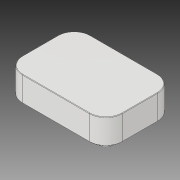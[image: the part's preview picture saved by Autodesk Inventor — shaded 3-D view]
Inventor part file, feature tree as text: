
AUTODESK INVENTOR PART (.ipt)
format: ipt  version: 2018 (Build 220112000, 112)  size: 356,352 bytes
history: native  units: mm
features: extrude x3, sketch x3, fillet x2, plane x2, mirror x2, other x1
ambient origin geometry x8: Origin, YZ Plane, XZ Plane, XY Plane, X Axis, Y Axis, Z Axis, Center Point
bodies: Solid1 (feature_tree)
feature tree (13):
  extrude  "Extrusion1"  Depth=75.0mm
  fillet  "Fillet1"  Radius=27.5mm
  extrude  "Extrusion2"  Depth=110.0mm
  extrude  "Extrusion3"  Depth=0.5mm
  plane  "Work Plane1"
  plane  "Work Plane2"
  mirror  "Mirror1"
  mirror  "Mirror2"
  fillet  "Fillet2"  Radius=0.5mm
  sketch  "Sketch1"  dims[d0=110.0mm d1=75.0mm d2=27.5mm d3=0.0mm]
  sketch  "Sketch2"  dims[d4=18.0mm d14=110.0mm]
  other  "Image1"
  sketch  "Sketch3"  dims[d26=2.0mm d27=0.0mm d28=12.5mm d29=0.5mm d30=0.0mm d31=0.5mm]
